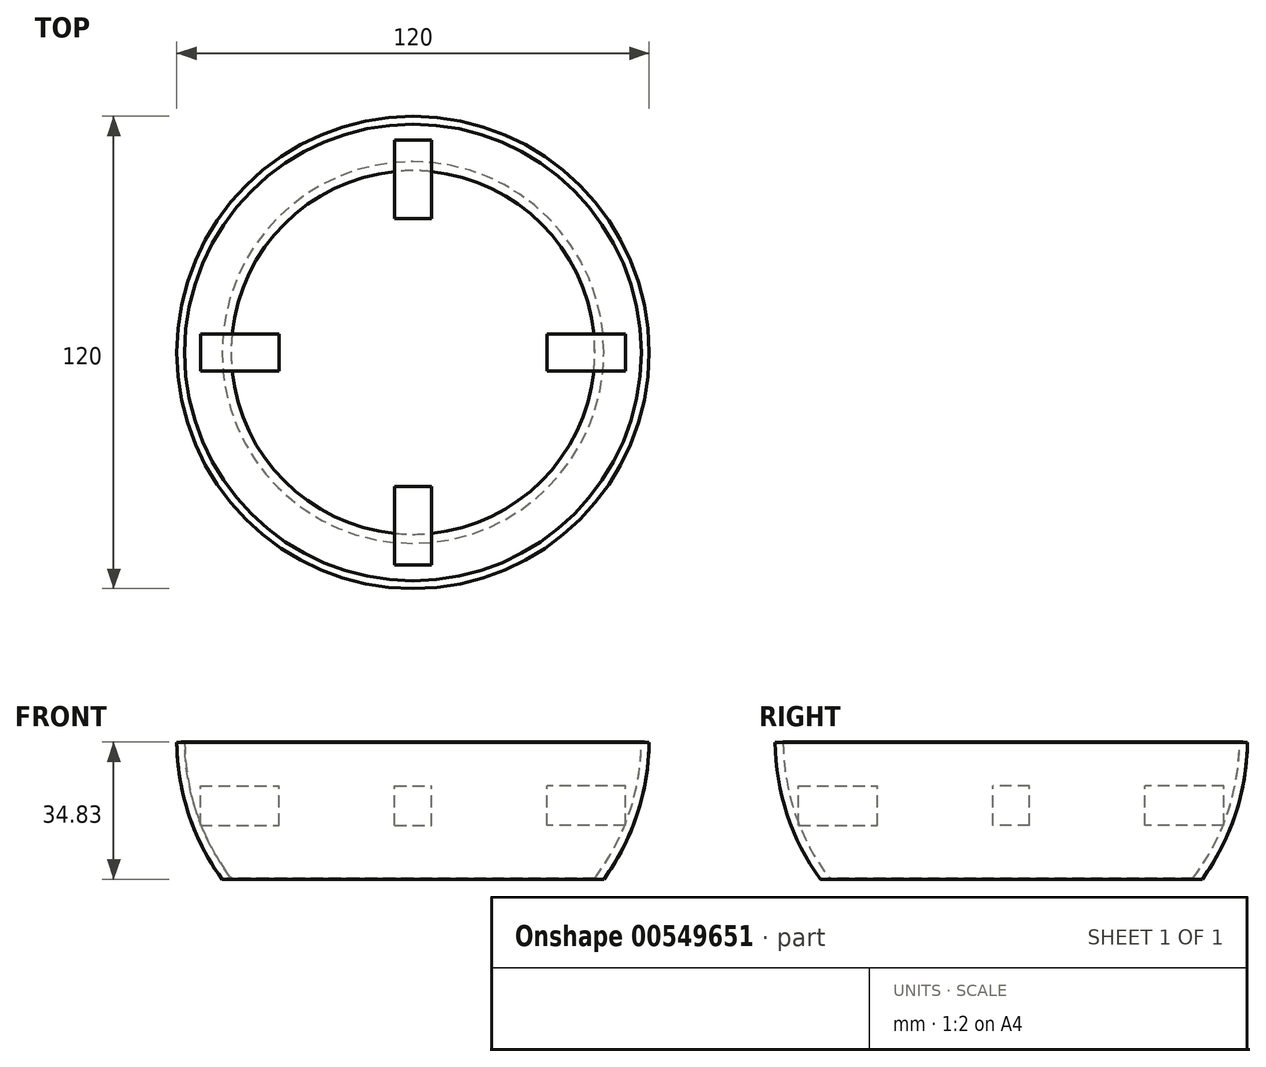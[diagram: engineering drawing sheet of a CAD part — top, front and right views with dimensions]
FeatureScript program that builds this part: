
annotation { "Feature Type Name" : "Feature", "Feature Type Description" : "" }
export const myFeature = defineFeature(function(context is Context, id is Id, definition is map)
    precondition{}
    {
        {
            var Q0;
            Q0=qCreatedBy(makeId("Top.planeOp"),FACE);
            var sketch = newSketch(context, id + "F0", { "sketchPlane" : qUnion([Q0])});
            skLineSegment(sketch, "E0.bottom", {"start": v(4.67, 54) * mm, "end": v(-4.68, 54) * mm});
            skLineSegment(sketch, "E0.top", {"start": v(4.68, 34) * mm, "end": v(-4.67, 34) * mm});
            skLineSegment(sketch, "E0.left", {"start": v(4.68, 54) * mm, "end": v(4.68, 34) * mm});
            skLineSegment(sketch, "E0.right", {"start": v(-4.67, 54) * mm, "end": v(-4.67, 34) * mm});
            skPoint(sketch, "E0.middle", {"position": v(0, 44) * mm});
            skSolve(sketch);
        }
        {
            var Q0;
            Q0=qCreatedBy(makeId("Right.planeOp"),FACE);
            var sketch = newSketch(context, id + "F1", { "sketchPlane" : qUnion([Q0])});
            skLineSegment(sketch, "E1", {"start": v(0, 0) * mm, "end": v(0, -40) * mm});
            skSolve(sketch);
        }
        {
            var Q0;
            Q0=qCreatedBy(makeId("Right.planeOp"),FACE);
            var sketch = newSketch(context, id + "F2", { "sketchPlane" : qUnion([Q0])});
            skCircle(sketch, "E2", {"center": v(0, 11.65) * mm, "radius": 60 * mm, "construction": true});
            skSolve(sketch);
        }
        {
            var Q0;
            Q0=qCreatedBy(makeId("Right.planeOp"),FACE);
            var sketch = newSketch(context, id + "F3", { "sketchPlane" : qUnion([Q0])});
            skLineSegment(sketch, "E3", {"start": v(0, 43.23) * mm, "end": v(0, 10.88) * mm});
            skSolve(sketch);
        }
        {
            var Q0;
            Q0=qCreatedBy(makeId("Right.planeOp"),FACE);
            var sketch = newSketch(context, id + "F4", { "sketchPlane" : qUnion([Q0])});
            skArc(sketch, "E4", {"start": v(-58, 11.14) * mm, "mid": v(-54.89, -7.1) * mm, "end": v(-46.2, -23.43) * mm});
            skArc(sketch, "E5", {"start": v(-60, 11.1) * mm, "mid": v(-56.97, -7.2) * mm, "end": v(-48.5, -23.69) * mm});
            skLineSegment(sketch, "E6", {"start": v(-46.2, -23.43) * mm, "end": v(-48.5, -23.69) * mm});
            skLineSegment(sketch, "E7", {"start": v(-58, 11.14) * mm, "end": v(-60, 11.1) * mm});
            skSolve(sketch);
        }
        {
            var Q0;
            Q0=qSketchRegion(id+"F4",true);
            var Q1;
            Q1=sQuery(id+"F3.wireOp",EDGE,"E3");
            revolve(context, id + "F5", {"entities" : qUnion([Q0]), "axis" : qUnion([Q1]), "revolveType" : RevolveType.FULL});
        }
        {
            var Q0;
            Q0=makeQuery(id+"F5.opRevolve","SWEPT_BODY",BODY,{"disambiguationData":[OSD([sQuery(id+"F4.wireOp",EDGE,"E4"),sQuery(id+"F4.wireOp",EDGE,"E5"),sQuery(id+"F4.wireOp",EDGE,"E6"),sQuery(id+"F4.wireOp",EDGE,"E7")])]});
            var Q1;
            Q1=sQuery(id+"F3.wireOp",EDGE,"E3");
            circularPattern(context, id + "F6", {"entities" : qUnion([Q0]), "axis" : qUnion([Q1]), "angle" : 360 * degree, "instanceCount" : 4, "equalSpace" : true});
        }
        {
            var Q0;
            Q0=makeQuery(id+"F6.opPattern","COPY",EDGE,{"derivedFrom":makeQuery(id+"F5.opRevolve","SWEPT_EDGE",EDGE,{"disambiguationData":[OSD([sQuery(id+"F4.wireOp",EDGE,"E4"),sQuery(id+"F4.wireOp",EDGE,"E6")])]}),"instanceName":"1"});
            fillet(context, id + "F7", {"entities" : qUnion([Q0]), "radius" : 4 * mm, "tangentPropagation" : true, "allowEdgeOverflow" : false});
        }
        {
            var Q0;
            Q0 = qSketchRegion(id + "F0", true);
            extrude(context, id + "F8", {"entities" : qUnion([Q0]), "oppositeDirection" : true, "depth" : 10 * mm, "offsetDistance" : 25 * mm});
        }
        {
            var Q0;
            Q0=makeQuery(id+"F8.opExtrude","SWEPT_BODY",BODY,{"disambiguationData":[OSD([sQuery(id+"F0.wireOp",EDGE,"E0.bottom"),sQuery(id+"F0.wireOp",EDGE,"E0.top"),sQuery(id+"F0.wireOp",EDGE,"E0.left"),sQuery(id+"F0.wireOp",EDGE,"E0.right")])]});
            var Q1;
            Q1=sQuery(id+"F1.wireOp",EDGE,"E1");
            circularPattern(context, id + "F9", {"entities" : qUnion([Q0]), "axis" : qUnion([Q1]), "angle" : 360 * degree, "instanceCount" : 4, "equalSpace" : true});
        }
        {
            var Q0;
            Q0=makeQuery(id+"F6.opPattern","COPY",BODY,{"derivedFrom":makeQuery(id+"F5.opRevolve","SWEPT_BODY",BODY,{"disambiguationData":[OSD([sQuery(id+"F4.wireOp",EDGE,"E4"),sQuery(id+"F4.wireOp",EDGE,"E5"),sQuery(id+"F4.wireOp",EDGE,"E6"),sQuery(id+"F4.wireOp",EDGE,"E7")])]}),"instanceName":"1"});
            deleteBodies(context, id + "F10", {"entities" : qUnion([Q0])});
        }
    });
